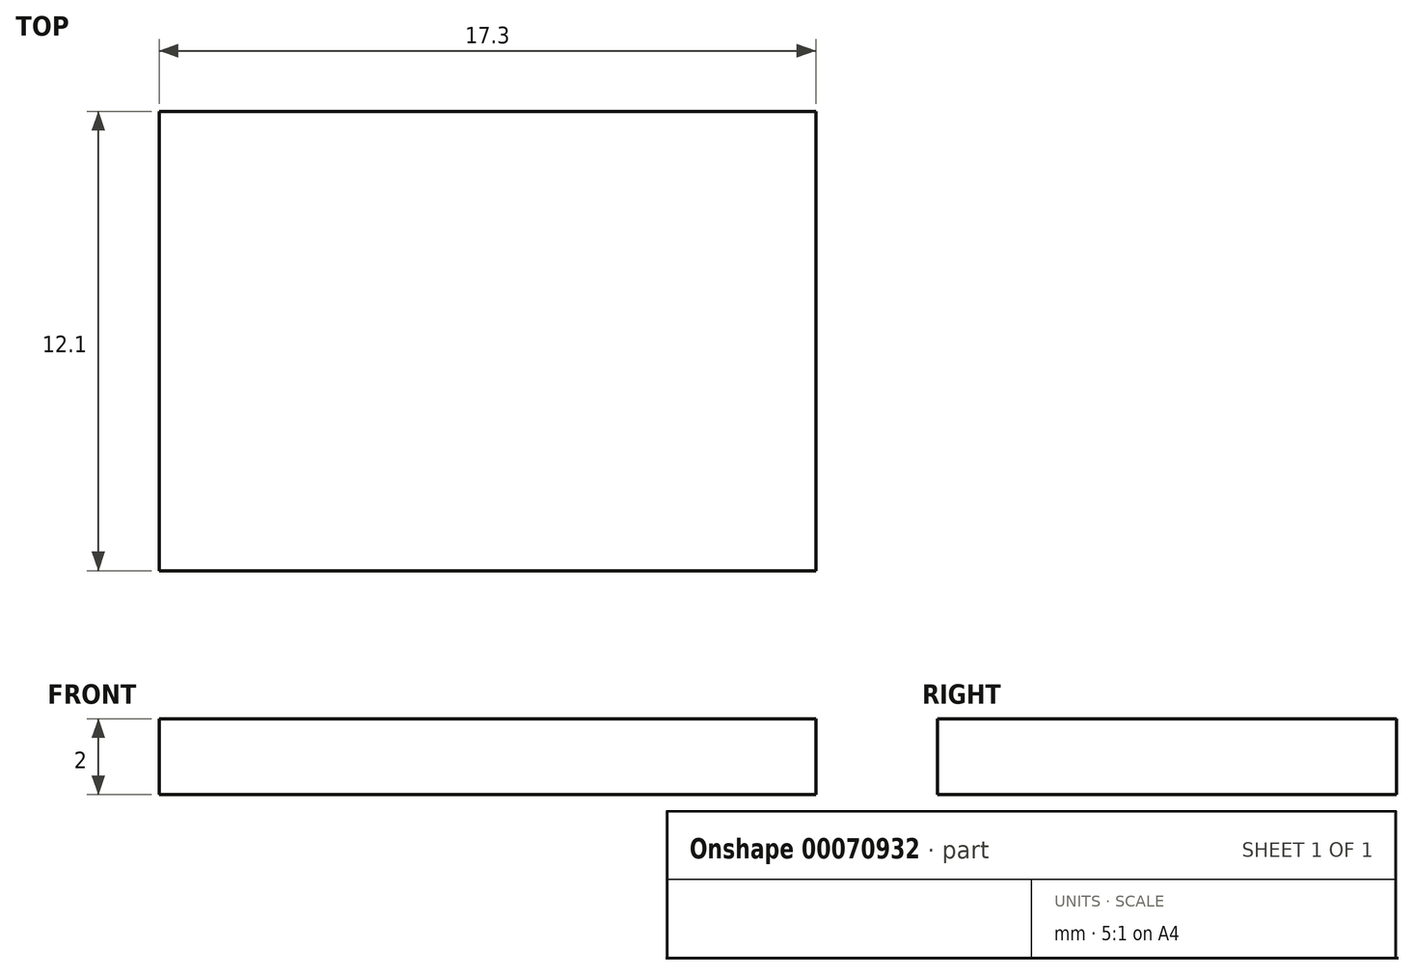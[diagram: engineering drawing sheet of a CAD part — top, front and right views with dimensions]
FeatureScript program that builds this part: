
annotation { "Feature Type Name" : "Feature", "Feature Type Description" : "" }
export const myFeature = defineFeature(function(context is Context, id is Id, definition is map)
    precondition{}
    {
        {
            var Q0;
            Q0=qCreatedBy(makeId("Top.planeOp"),FACE);
            var sketch = newSketch(context, id + "F0", { "sketchPlane" : qUnion([Q0])});
            skLineSegment(sketch, "E0.rect.bottom", {"start": v(-8.65, 6.05) * mm, "end": v(8.65, 6.05) * mm});
            skLineSegment(sketch, "E0.rect.top", {"start": v(-8.65, -6.05) * mm, "end": v(8.65, -6.05) * mm});
            skLineSegment(sketch, "E0.rect.left", {"start": v(-8.65, 6.05) * mm, "end": v(-8.65, -6.05) * mm});
            skLineSegment(sketch, "E0.rect.right", {"start": v(8.65, 6.05) * mm, "end": v(8.65, -6.05) * mm});
            skPoint(sketch, "E0.rect.middle", {"position": v(0, 0) * mm});
            skSolve(sketch);
        }
        {
            var Q0;
            Q0 = qSketchRegion(id + "F0", true);
            extrude(context, id + "F1", {"entities" : qUnion([Q0]), "depth" : 2 * mm});
        }
    });
